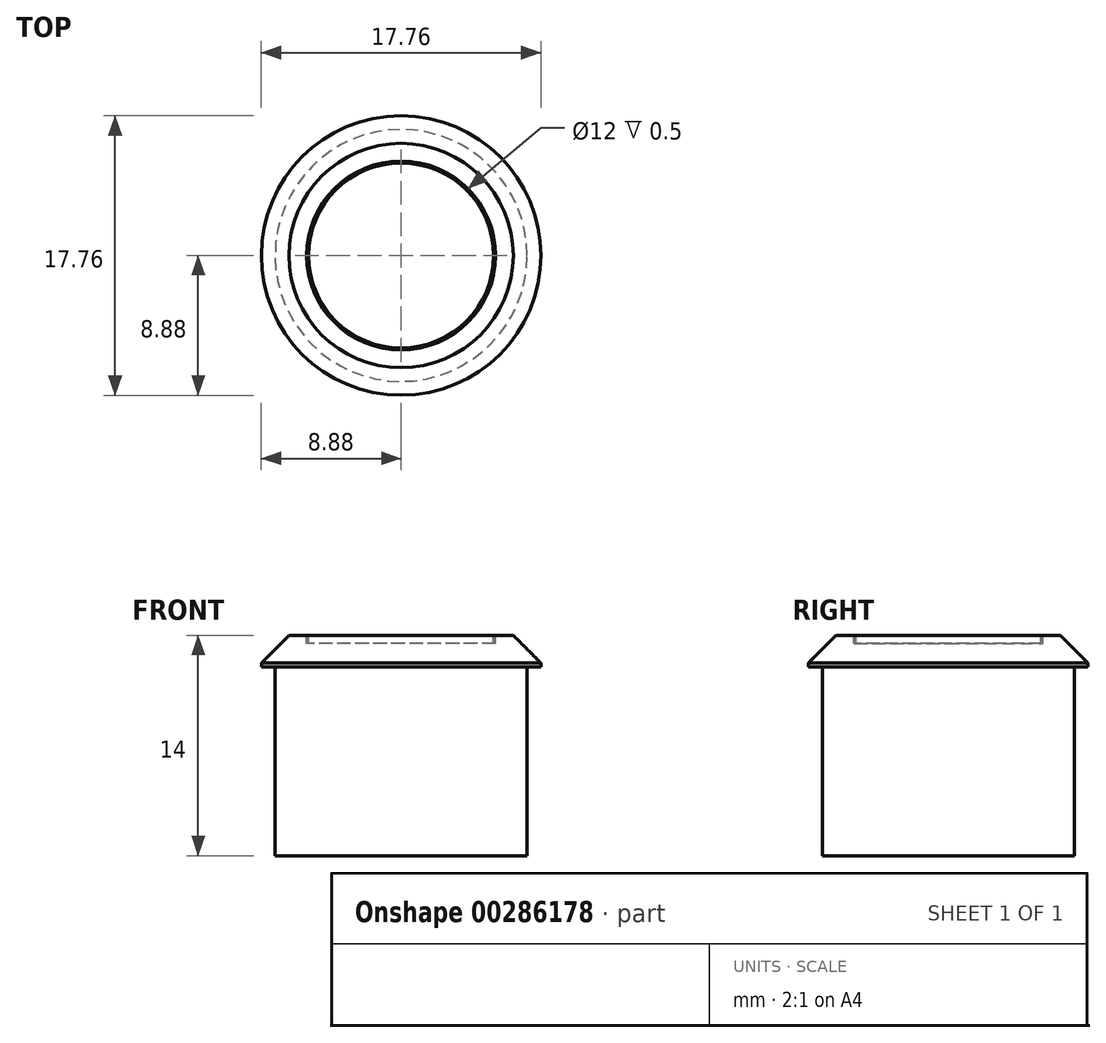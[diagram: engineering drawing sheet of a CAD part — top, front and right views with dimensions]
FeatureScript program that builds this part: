
annotation { "Feature Type Name" : "Feature", "Feature Type Description" : "" }
export const myFeature = defineFeature(function(context is Context, id is Id, definition is map)
    precondition{}
    {
        {
            var Q0;
            Q0=qCreatedBy(makeId("Top.planeOp"),FACE);
            var sketch = newSketch(context, id + "F0", { "sketchPlane" : qUnion([Q0])});
            skCircle(sketch, "E0", {"center": v(0, 0) * mm, "radius": 8 * mm});
            skSolve(sketch);
        }
        {
            var Q0;
            Q0=makeQuery(id+"F0.imprint","IMPRINT",FACE,{"disambiguationData":[TD([[makeQuery(id+"F0.imprint","IMPRINT",EDGE,{"derivedFrom":sQuery(id+"F0.wireOp",EDGE,"E0")}),1.0]])]});
            extrude(context, id + "F1", {"entities" : qUnion([Q0]), "depth" : 12 * mm});
        }
        {
            var Q0;
            Q0=makeQuery(id+"F1.opExtrude","CAP_FACE",FACE,{"disambiguationData":[OSD([sQuery(id+"F0.wireOp",EDGE,"E0")])],"isStart":false});
            var sketch = newSketch(context, id + "F2", { "sketchPlane" : qUnion([Q0])});
            skCircle(sketch, "E1", {"center": v(0, 0) * mm, "radius": 8.88 * mm});
            skSolve(sketch);
        }
        {
            var Q0;
            Q0=makeQuery(id+"F2.imprint","IMPRINT",FACE,{"disambiguationData":[TD([[makeQuery(id+"F2.imprint","IMPRINT",EDGE,{"derivedFrom":sQuery(id+"F2.wireOp",EDGE,"E1")}),1.0]])]});
            var Q1;
            Q1=makeQuery(id+"F2.imprint","IMPRINT",FACE,{"disambiguationData":[TD([[makeQuery(id+"F2.imprint","IMPRINT",EDGE,{"derivedFrom":makeQuery(id+"F1.opExtrude","CAP_EDGE",EDGE,{"disambiguationData":[OSD([sQuery(id+"F0.wireOp",EDGE,"E0")])],"isStart":false})}),1.0]])]});
            extrude(context, id + "F3", {"entities" : qUnion([Q0, Q1]), "operationType" : NewBodyOperationType.ADD, "depth" : 2 * mm});
        }
        {
            var Q0;
            Q0=makeQuery(id+"F3.opExtrude","CAP_EDGE",EDGE,{"disambiguationData":[OSD([sQuery(id+"F2.wireOp",EDGE,"E1")])],"isStart":false});
            chamfer(context, id + "F4", {"entities" : qUnion([Q0]), "width" : 1.75 * mm, "tangentPropagation" : true});
        }
        {
            var Q0;
            Q0=makeQuery(id+"F3.opExtrude","CAP_FACE",FACE,{"disambiguationData":[OSD([sQuery(id+"F2.wireOp",EDGE,"E1")])],"isStart":false});
            var sketch = newSketch(context, id + "F5", { "sketchPlane" : qUnion([Q0])});
            skCircle(sketch, "E2", {"center": v(0, 0) * mm, "radius": 5.88 * mm});
            skCircle(sketch, "E3", {"center": v(0, 0) * mm, "radius": 6 * mm});
            skSolve(sketch);
        }
        {
            var Q0;
            Q0=makeQuery(id+"F5.imprint","IMPRINT",FACE,{"disambiguationData":[TD([[makeQuery(id+"F5.imprint","IMPRINT",EDGE,{"derivedFrom":sQuery(id+"F5.wireOp",EDGE,"E2")}),-1.0]])]});
            extrude(context, id + "F6", {"entities" : qUnion([Q0]), "operationType" : NewBodyOperationType.REMOVE, "oppositeDirection" : true, "depth" : .5 * mm});
        }
    });
